# Revit family: IS_Flushplate_Multiproduct_BIM_GB_VV6398;VV6400;VV6410
name_source: partatom
category: Plumbing Fixtures
revit_build: Autodesk Revit MEP 2012 (Build: 20110309_2315(x64)
units: mm (PartAtom-declared; Revit-internal decimal feet)

## types (6) — shared parameters
Accessories = www.idealspec.co.uk
Assembly Code = C1030200
AssetType = Fixed
BIMObjectName = FLUSHMECHANISM_IdealStandard_InWallSystemFlushPlates_AllVariants
BREEAM = No
Category = SanitaryTerminal_CISTERN_UK
ConnectionType = Pneumatic
CurrentRevision = 1
Default Elevation = 1219 mm
DurationUnit = Years
ECA = No
Help = http://www.idealspec.co.uk
InstallationDate = 0
InstallationInstructions = http://www.idealspec.co.uk
MaintenanceInformation = http://www.idealspec.co.uk
Manufacturer = Ideal Standard Ltd
ManufacturerURL = www.idealspec.co.uk
NBSReference = 300
Name = FLUSHMECHANISM_IdealStandard_InWallSystemFlushPlates_AllVariants
NominalHeight = 10 mm  [stored 0.0328084 ft]
NominalLength = 215 mm
NominalWidth = 145 mm  [stored 0.475722 ft]
ProductDataSheet = http://www.idealspec.co.uk
ProductInformation = http://www.idealspec.co.uk
SalesInformation = http://www.idealspec.co.uk
SendEnquiry = http://www.idealspec.co.uk
Shape = Rectangular
Space = Internal
SpareParts = www.fastpart-spares.co.uk
TMV3 = No
URL = http://www.idealspec.co.uk
Version = 1
WRAS = No
WarrantyDescription = Manufacturers Warranty
WarrantyDurationParts = 5
WarrantyDurationUnit = Years
WarrantyGuarantorParts = Ideal Standard Ltd
WarrantyInformation = http://www.idealspec.co.uk
WaterEfficientProduct = No

## per-type parameters (varying)
| type | Color | Description | Features | Finish | Material | Model | ModelNumber | ModelReference | PartNumber | Size | VV6398 | VV6400 | VV6410 |
| VV639864 - Trend stainless steel flush plate, dual flush, pnuematic with tamper resistant screws - Chrome | Chrome | Trend stainless steel flush plate, dual flush, pnuematic with tamper resistant screws | stainless steel flush plate, dual flush, pnuematic with tamper resistant screws | Chrome | Stainless Steel | VV639864 | VV639864 | VV639864 | VV639864 | 215mm x 145mm x 2mm | Yes | No | No |
| VV639866 - Trend stainless steel flush plate, dual flush, pnuematic with tamper resistant screws - Satin | Satin | Trend stainless steel flush plate, dual flush, pnuematic with tamper resistant screws | stainless steel flush plate, dual flush, pnuematic with tamper resistant screws | Satin | Stainless Steel | VV639866 | VV639866 | VV639866 | VV639866 | 215mm x 145mm x 2mm | Yes | No | No |
| VV640084 - Salina flush plate, dual flush, pnuematic - Chrome | Chrome | Salina flush plate, dual flush, pnuematic | flush plate, dual flush, pnuematic | Chrome | ABS | VV640084 | VV640084 | VV640084 | VV640084 | 215mm x 145mm x 10mm | No | Yes | No |
| VV640086 - Salina flush plate, dual flush, pnuematic - Satin | Satin | Salina flush plate, dual flush, pnuematic | flush plate, dual flush, pnuematic | Satin | ABS | VV640086 | VV640086 | VV640086 | VV640086 | 215mm x 145mm x 10mm | No | Yes | No |
| VV641004 - Karisma flush plate, dual flush, pneumatic - Chrome | Chrome | Karisma flush plate, dual flush, pneumatic | flush plate, dual flush, pnuematic | Chrome | ABS | VV641004 | VV641004 | VV641004 | VV641004 | 215mm x 145mm x 10mm | No | No | Yes |
| VV641006 - Karisma flush plate, dual flush, pneumatic - Satin | Satin | Karisma flush plate, dual flush, pneumatic | flush plate, dual flush, pnuematic | Satin | ABS | VV641006 | VV641006 | VV641006 | VV641006 | 215mm x 145mm x 10mm | No | No | Yes |

note: [stored X ft] marks values corroborated as IEEE doubles in the binary element streams (Revit-internal decimal feet)

## geometry (parser evidence)
native form markers: Blend x4, Sweep x1
no freeform markers — native parametric forms only
